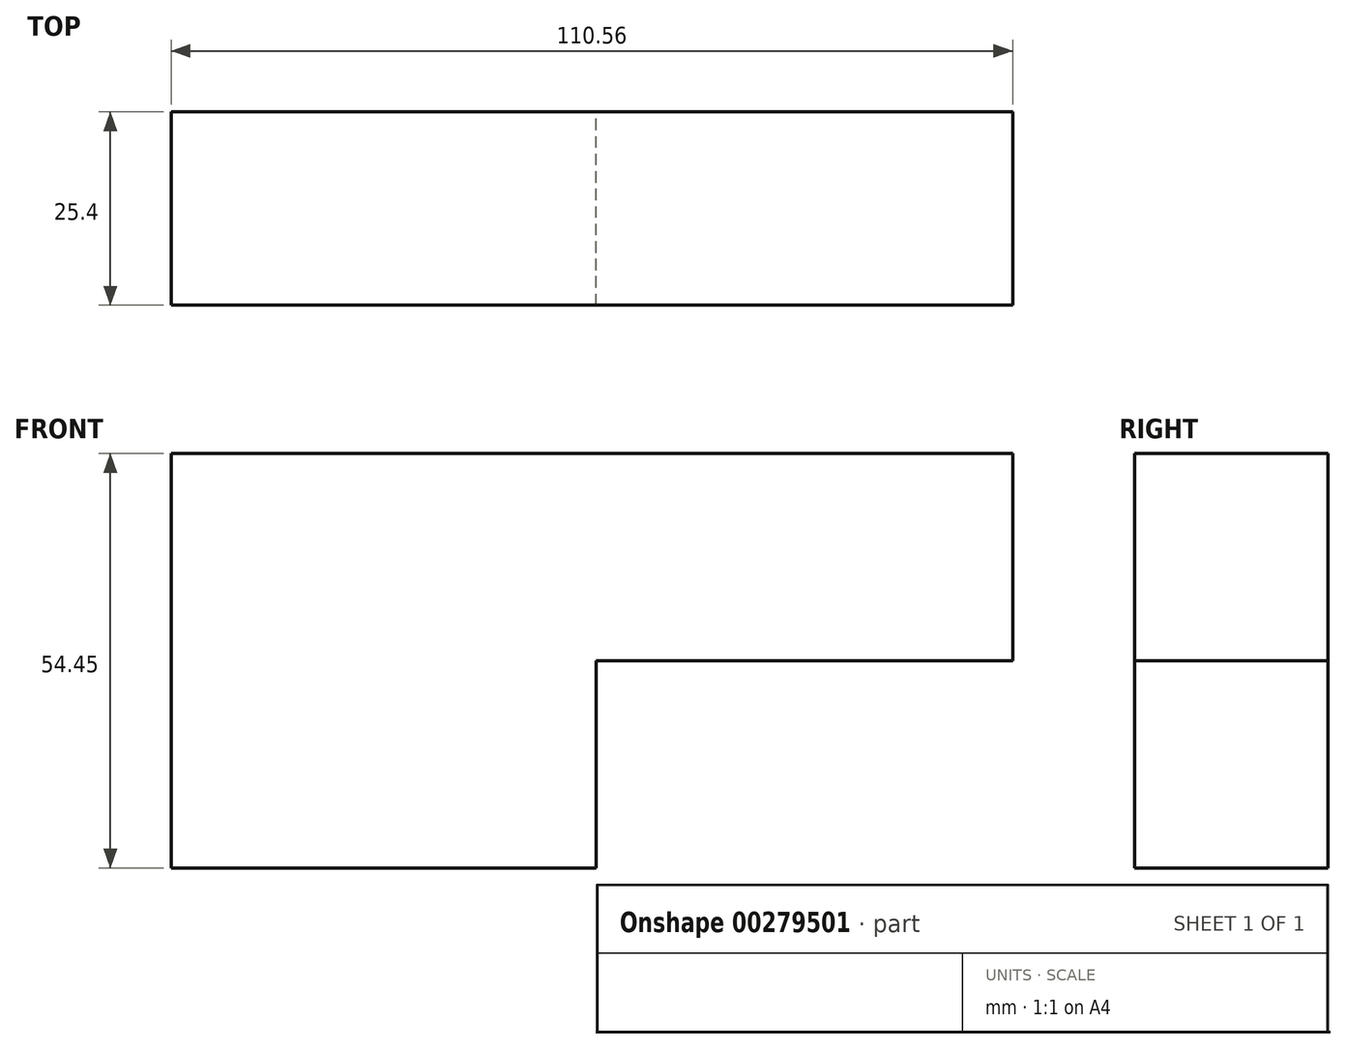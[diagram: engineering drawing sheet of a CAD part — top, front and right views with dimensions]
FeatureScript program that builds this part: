
annotation { "Feature Type Name" : "Feature", "Feature Type Description" : "" }
export const myFeature = defineFeature(function(context is Context, id is Id, definition is map)
    precondition{}
    {
        {
            var Q0;
            Q0=qCreatedBy(makeId("Front.planeOp"),FACE);
            var sketch = newSketch(context, id + "F0", { "sketchPlane" : qUnion([Q0])});
            skLineSegment(sketch, "E0.bottom", {"start": v(-55.83, 0) * mm, "end": v(54.73, 0) * mm});
            skLineSegment(sketch, "E0.top", {"start": v(-55.83, 54.45) * mm, "end": v(54.73, 54.45) * mm});
            skLineSegment(sketch, "E0.left", {"start": v(-55.83, 0) * mm, "end": v(-55.83, 54.45) * mm});
            skLineSegment(sketch, "E0.right", {"start": v(54.73, 0) * mm, "end": v(54.73, 54.45) * mm});
            skLineSegment(sketch, "E1.bottom", {"start": v(54.73, 27.23) * mm, "end": v(0, 27.23) * mm});
            skLineSegment(sketch, "E1.top", {"start": v(54.73, 0) * mm, "end": v(0, 0) * mm});
            skLineSegment(sketch, "E1.left", {"start": v(54.73, 27.23) * mm, "end": v(54.73, 0) * mm});
            skLineSegment(sketch, "E1.right", {"start": v(0, 27.23) * mm, "end": v(0, 0) * mm});
            skSolve(sketch);
        }
        {
            var Q0;
            Q0=qCreatedBy(makeId("Front.planeOp"),FACE);
            var sketch = newSketch(context, id + "F1", { "sketchPlane" : qUnion([Q0])});
            skLineSegment(sketch, "E2.0.0", {"start": v(0, 0) * mm, "end": v(0, 27.23) * mm});
            skLineSegment(sketch, "E2.0.1", {"start": v(0, 27.23) * mm, "end": v(54.73, 27.23) * mm});
            skLineSegment(sketch, "E2.0.2", {"start": v(54.73, 27.23) * mm, "end": v(54.73, 54.45) * mm});
            skLineSegment(sketch, "E2.0.3", {"start": v(54.73, 54.45) * mm, "end": v(-55.83, 54.45) * mm});
            skLineSegment(sketch, "E2.0.4", {"start": v(-55.83, 54.45) * mm, "end": v(-55.83, 0) * mm});
            skLineSegment(sketch, "E2.0.5", {"start": v(-55.83, 0) * mm, "end": v(0, 0) * mm});
            skSolve(sketch);
        }
        {
            var Q0;
            Q0 = qSketchRegion(id + "F1", true);
            extrude(context, id + "F3", {"entities" : qUnion([Q0]), "depth" : 25.4 * mm});
        }
    });
